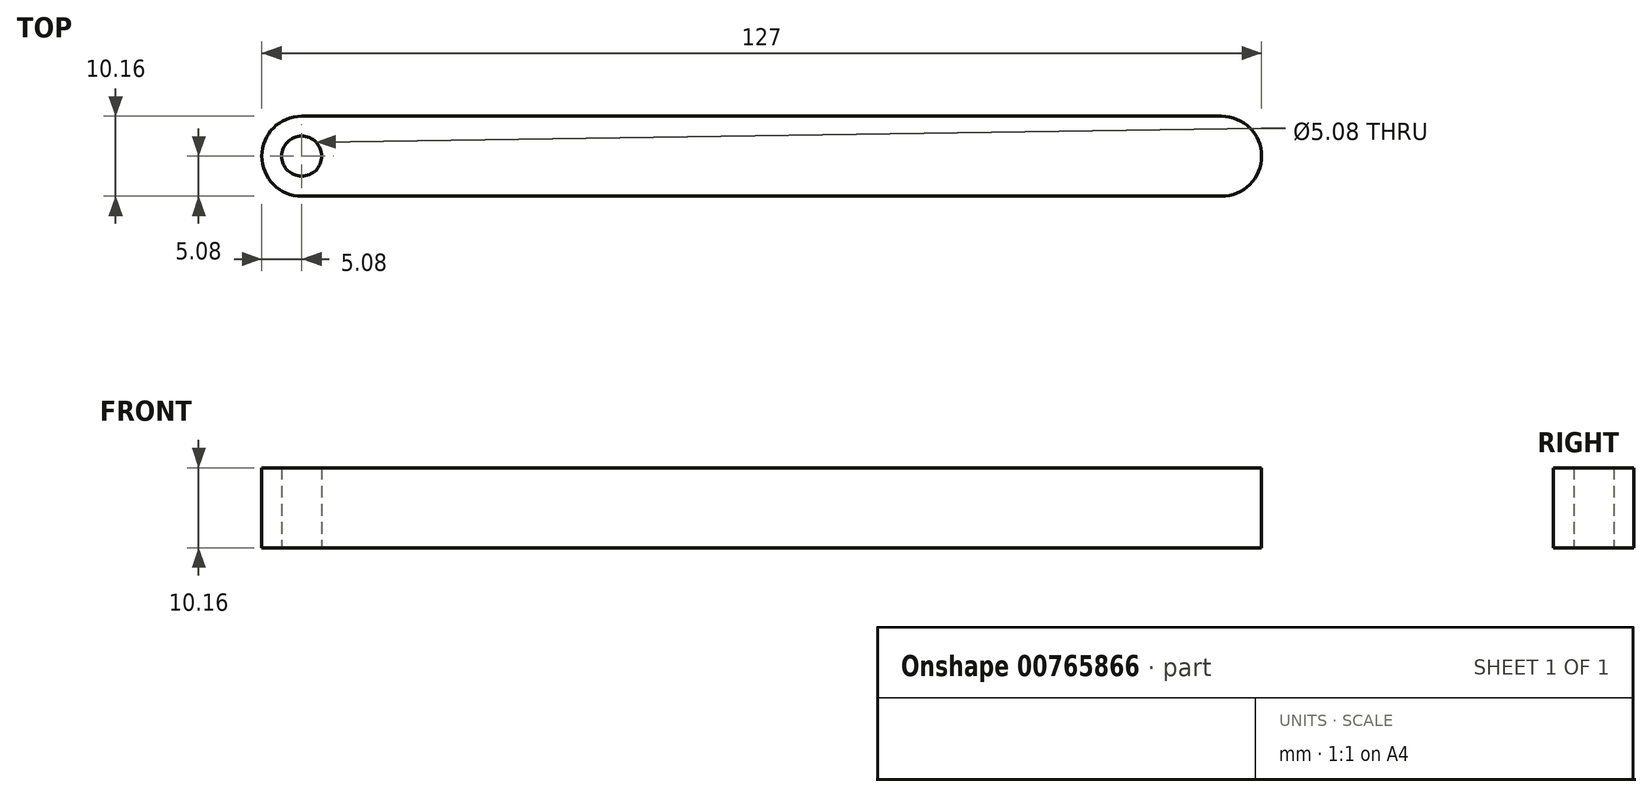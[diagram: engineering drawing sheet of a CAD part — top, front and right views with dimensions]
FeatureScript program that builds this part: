
annotation { "Feature Type Name" : "Feature", "Feature Type Description" : "" }
export const myFeature = defineFeature(function(context is Context, id is Id, definition is map)
    precondition{}
    {
        {
            var Q0;
            Q0=qCreatedBy(makeId("Top.planeOp"),FACE);
            var sketch = newSketch(context, id + "F0", { "sketchPlane" : qUnion([Q0])});
            skLineSegment(sketch, "E0.bottom", {"start": v(-63.5, -5.08) * mm, "end": v(63.5, -5.08) * mm});
            skLineSegment(sketch, "E0.top", {"start": v(-63.5, 5.08) * mm, "end": v(63.5, 5.08) * mm});
            skLineSegment(sketch, "E0.left", {"start": v(-63.5, -5.08) * mm, "end": v(-63.5, 5.08) * mm});
            skLineSegment(sketch, "E0.right", {"start": v(63.5, -5.08) * mm, "end": v(63.5, 5.08) * mm});
            skSolve(sketch);
        }
        {
            var Q0;
            Q0=makeQuery(id+"F0.imprint","IMPRINT",FACE,{"disambiguationData":[TD([[makeQuery(id+"F0.imprint","IMPRINT",EDGE,{"derivedFrom":sQuery(id+"F0.wireOp",EDGE,"E0.bottom")}),1.0]])]});
            extrude(context, id + "F1", {"entities" : qUnion([Q0]), "depth" : 10.16 * mm, "offsetDistance" : 25.4 * mm});
        }
        {
            var Q0;
            Q0=makeQuery(id+"F1.opExtrude","SWEPT_EDGE",EDGE,{"disambiguationData":[OSD([sQuery(id+"F0.wireOp",EDGE,"E0.bottom"),sQuery(id+"F0.wireOp",EDGE,"E0.left")])]});
            var Q1;
            Q1=makeQuery(id+"F1.opExtrude","SWEPT_EDGE",EDGE,{"disambiguationData":[OSD([sQuery(id+"F0.wireOp",EDGE,"E0.top"),sQuery(id+"F0.wireOp",EDGE,"E0.left")])]});
            var Q2;
            Q2=makeQuery(id+"F1.opExtrude","SWEPT_EDGE",EDGE,{"disambiguationData":[OSD([sQuery(id+"F0.wireOp",EDGE,"E0.bottom"),sQuery(id+"F0.wireOp",EDGE,"E0.right")])]});
            var Q3;
            Q3=makeQuery(id+"F1.opExtrude","SWEPT_EDGE",EDGE,{"disambiguationData":[OSD([sQuery(id+"F0.wireOp",EDGE,"E0.top"),sQuery(id+"F0.wireOp",EDGE,"E0.right")])]});
            fillet(context, id + "F2", {"entities" : qUnion([Q0, Q1, Q2, Q3]), "radius" : 5.08 * mm, "tangentPropagation" : true, "allowEdgeOverflow" : false});
        }
        {
            var Q0;
            Q0=makeQuery(id+"F1.opExtrude","CAP_FACE",FACE,{"disambiguationData":[OSD([sQuery(id+"F0.wireOp",EDGE,"E0.bottom"),sQuery(id+"F0.wireOp",EDGE,"E0.top"),sQuery(id+"F0.wireOp",EDGE,"E0.left"),sQuery(id+"F0.wireOp",EDGE,"E0.right")])],"isStart":true});
            var sketch = newSketch(context, id + "F3", { "sketchPlane" : qUnion([Q0])});
            skCircle(sketch, "E1", {"center": v(-58.42, 0) * mm, "radius": 2.54 * mm});
            skSolve(sketch);
        }
        {
            var Q0;
            Q0=makeQuery(id+"F3.imprint","IMPRINT",FACE,{"disambiguationData":[TD([[makeQuery(id+"F3.imprint","IMPRINT",EDGE,{"derivedFrom":sQuery(id+"F3.wireOp",EDGE,"E1")}),1.0]])]});
            extrude(context, id + "F4", {"entities" : qUnion([Q0]), "operationType" : NewBodyOperationType.REMOVE, "oppositeDirection" : true, "depth" : 25.4 * mm, "offsetDistance" : 25.4 * mm});
        }
    });
